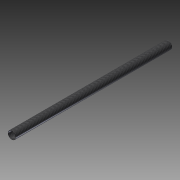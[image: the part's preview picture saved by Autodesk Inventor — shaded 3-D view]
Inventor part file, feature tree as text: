
AUTODESK INVENTOR PART (.ipt)
format: ipt  version: 2015 (Build 190159000, 159)  size: 89,600 bytes
history: native  units: in
note: dims shown in document units (in); Inventor stores cm internally (conversion verified against a paired STEP export)
features: extrude x1, sketch x1
ambient origin geometry x8: Origin, YZ Plane, XZ Plane, XY Plane, X Axis, Y Axis, Z Axis, Center Point
bodies: Solid1 (feature_tree)
feature tree (2):
  extrude  "Extrusion1"  Depth=0.4528in
  sketch  "Sketch1"  dims[d0=0.4921in d1=0.4528in d2=19.685in d3=0.0in]
